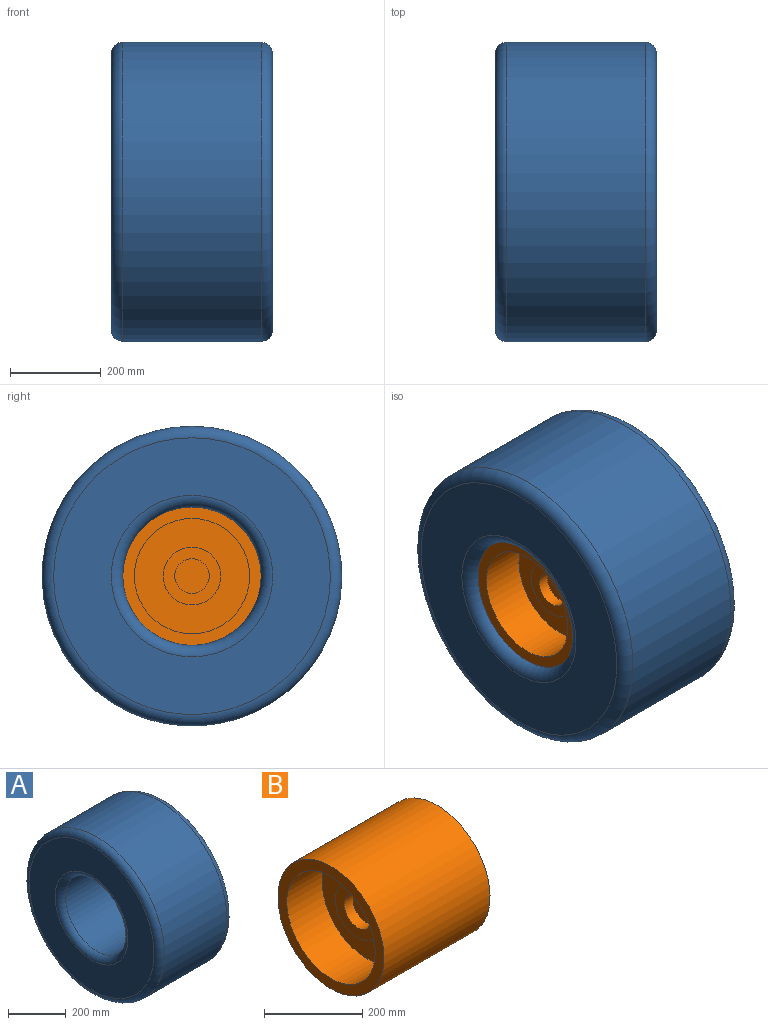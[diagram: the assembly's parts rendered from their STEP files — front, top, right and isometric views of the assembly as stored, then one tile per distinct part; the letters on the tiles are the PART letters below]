
ASSEMBLY  parts=2 mates=1
PART A: 8 faces, bbox 355.6x714.8x714.8 mm
  f0: cylinder r=152.4mm len=304.8mm, axis (-1,0,0), area 291863.5mm2, adj f4,f7
  f1: plane 609.6x609.6mm, normal (1,0,0), area 192548.8mm2, adj f4,f5
  f2: cylinder r=330.2mm len=660.4mm, axis (-1,0,0), area 632370.9mm2, adj f5,f6
  f3: plane 609.6x609.6mm, normal (-1,0,0), area 192548.8mm2, adj f6,f7
  f4: torus R=177.8mm, axis (-1,0,0), area 40518.7mm2, adj f0,f1
  f5: torus R=304.8mm, axis (-1,0,0), area 80463.3mm2, adj f1,f2
  f6: torus R=304.8mm, axis (-1,0,0), area 80463.3mm2, adj f2,f3
  f7: torus R=177.8mm, axis (-1,0,0), area 40518.7mm2, adj f0,f3
PART B: 15 faces, bbox 304.8x304.8x304.8 mm
  f0: cylinder r=76.2mm len=152.4mm, axis (1,0,0), area 60804.9mm2, adj f5,f6
  f1: cylinder r=152.4mm len=304.8mm, axis (-1,0,0), area 291863.5mm2, adj f2,f3
  f2: plane 304.8x304.8mm, normal (1,0,0), area 22295.1mm2, adj f1,f4
  f3: plane 304.8x304.8mm, normal (-1,0,0), area 22295.1mm2, adj f1,f10
  f4: cylinder r=127mm len=254mm, axis (1,0,0), area 141878.1mm2, adj f2,f5
  f5: plane 254x254mm, normal (1,0,0), area 32429.3mm2, adj f0,f4
  f6: plane 152.4x152.4mm, normal (1,0,0), area 5573.8mm2, adj f0,f8
  f7: plane 127x127mm, normal (1,0,0), area 12667.7mm2, adj f8
  f8: cylinder r=63.5mm len=127mm, axis (1,0,0), area 50670.7mm2, adj f6,f7
  f9: cylinder r=63.5mm len=127mm, axis (-1,0,0), area 10134.1mm2, adj f11,f12
  f10: cylinder r=127mm len=254mm, axis (-1,0,0), area 81073.2mm2, adj f3,f11
  f11: plane 254x254mm, normal (-1,0,0), area 38003.1mm2, adj f9,f10
  f12: plane 127x127mm, normal (-1,0,0), area 8107.3mm2, adj f9,f14
  f13: plane 76.2x76.2mm, normal (-1,0,0), area 4560.4mm2, adj f14
  f14: cylinder r=38.1mm len=76.2mm, axis (-1,0,0), area 6080.5mm2, adj f12,f13
PLACE A t=(571.22,0,0)mm
PLACE B t=(418.82,0,0)mm
MATE fastened B.f1 <-> A.f0  axis (-1,0,0) through (723.62,0,0)mm
